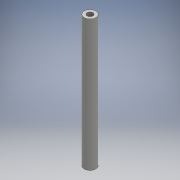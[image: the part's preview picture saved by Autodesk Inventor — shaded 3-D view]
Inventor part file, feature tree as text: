
AUTODESK INVENTOR PART (.ipt)
format: ipt  version: 2016 (Build 200138000, 138)  size: 89,600 bytes
history: native  units: mm
features: other x1, extrude x1, sketch x1
ambient origin geometry x8: Origin, YZ Plane, XZ Plane, XY Plane, X Axis, Y Axis, Z Axis, Center Point
bodies: Body1 (feature_tree)
feature tree (3):
  other  "ソリッド1"
  extrude  "押し出し1"  Depth=6.0mm
  sketch  "スケッチ1"
